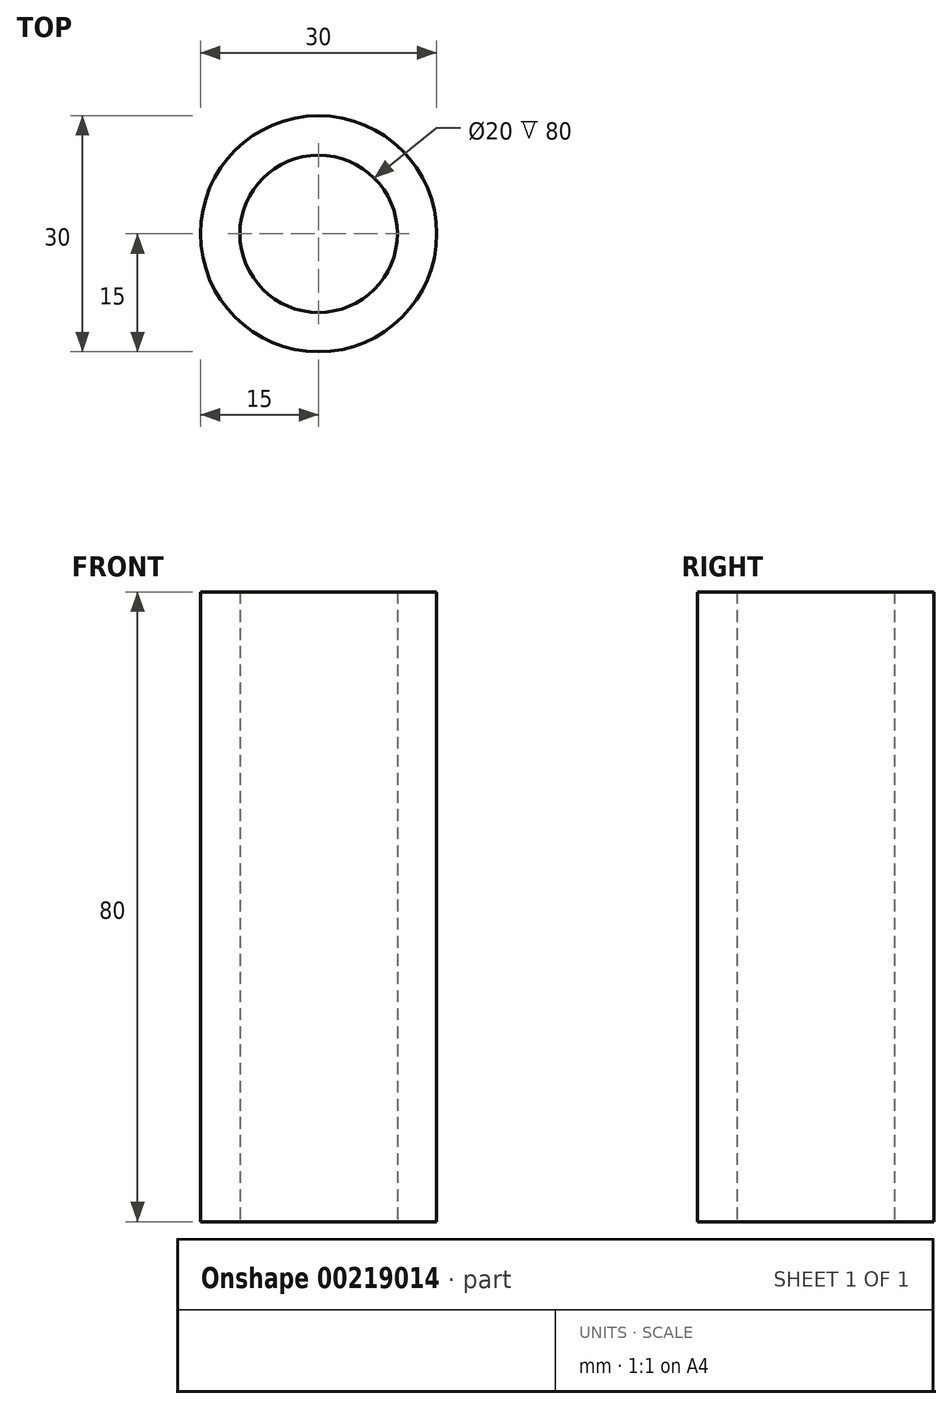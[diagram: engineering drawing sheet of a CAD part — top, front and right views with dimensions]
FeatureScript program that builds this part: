
annotation { "Feature Type Name" : "Feature", "Feature Type Description" : "" }
export const myFeature = defineFeature(function(context is Context, id is Id, definition is map)
    precondition{}
    {
        {
            var Q0;
            Q0=qCreatedBy(makeId("Top.planeOp"),FACE);
            var sketch = newSketch(context, id + "F0", { "sketchPlane" : qUnion([Q0])});
            skCircle(sketch, "E0", {"center": v(0, 0) * mm, "radius": 15 * mm});
            skSolve(sketch);
        }
        {
            var Q0;
            Q0=makeQuery(id+"F0.imprint","IMPRINT",FACE,{"disambiguationData":[TD([[makeQuery(id+"F0.imprint","IMPRINT",EDGE,{"derivedFrom":sQuery(id+"F0.wireOp",EDGE,"E0")}),1.0]])]});
            extrude(context, id + "F1", {"entities" : qUnion([Q0]), "depth" : 80 * mm});
        }
        {
            var Q0;
            Q0=makeQuery(id+"F1.opExtrude","CAP_FACE",FACE,{"disambiguationData":[OSD([sQuery(id+"F0.wireOp",EDGE,"E0")])],"isStart":true});
            var sketch = newSketch(context, id + "F2", { "sketchPlane" : qUnion([Q0])});
            skCircle(sketch, "E1", {"center": v(0, 0) * mm, "radius": 5 * mm});
            skSolve(sketch);
        }
        {
            var Q0;
            Q0=sQuery(id+"F2.wireOp",VERTEX,"E1.center");
            var Q1;
            Q1=makeQuery(id+"F1.opExtrude","SWEPT_BODY",BODY,{"disambiguationData":[OSD([sQuery(id+"F0.wireOp",EDGE,"E0")])]});
            hole(context, id + "F3", {"style" : HoleStyle.SIMPLE, "endStyle" : HoleEndStyle.THROUGH, "holeDiameter" : 20 * mm, "locations" : qUnion([Q0]), "scope" : qUnion([Q1]), "isTappedThrough" : true});
        }
        {
            var Q0;
            Q0=makeQuery(id+"F1.opExtrude","CAP_FACE",FACE,{"disambiguationData":[OSD([sQuery(id+"F0.wireOp",EDGE,"E0")])],"isStart":true});
            var sketch = newSketch(context, id + "F4", { "sketchPlane" : qUnion([Q0])});
            skCircle(sketch, "E2", {"center": v(0, 0) * mm, "radius": 9.68 * mm});
            skSolve(sketch);
        }
        {
            var Q0;
            Q0=makeQuery(id+"F4.imprint","IMPRINT",FACE,{"disambiguationData":[TD([[makeQuery(id+"F4.imprint","IMPRINT",EDGE,{"derivedFrom":makeQuery(id+"F1.opExtrude","CAP_EDGE",EDGE,{"disambiguationData":[OSD([sQuery(id+"F0.wireOp",EDGE,"E0")])],"isStart":true})}),-1.0]])]});
            var sketch = newSketch(context, id + "F5", { "sketchPlane" : qUnion([Q0])});
            skCircle(sketch, "E3", {"center": v(0, 0) * mm, "radius": 12.73 * mm});
            skSolve(sketch);
        }
        {
            var Q0;
            Q0=sQuery(id+"F5.wireOp",EDGE,"E3");
            var Q1;
            Q1=sQuery(id+"F4.wireOp",EDGE,"E2");
            extrude(context, id + "F6", {"bodyType" : ToolBodyType.SURFACE, "surfaceEntities" : qUnion([Q0, Q1]), "oppositeDirection" : true, "depth" : 5.33 * mm});
        }
    });
